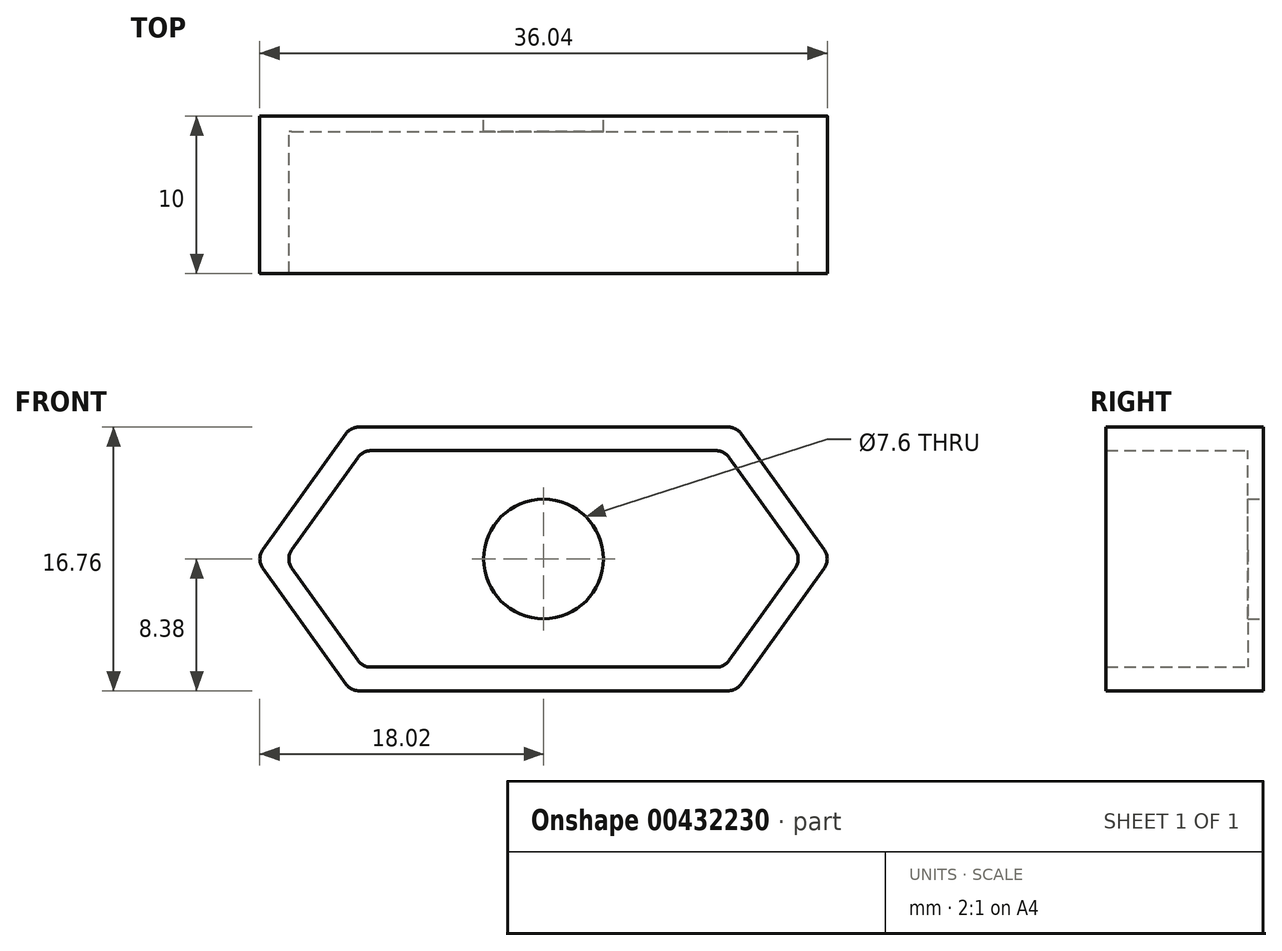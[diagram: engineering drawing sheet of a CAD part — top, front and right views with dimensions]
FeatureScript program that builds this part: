
annotation { "Feature Type Name" : "Feature", "Feature Type Description" : "" }
export const myFeature = defineFeature(function(context is Context, id is Id, definition is map)
    precondition{}
    {
        {
            var Q0;
            Q0=qCreatedBy(makeId("Front.planeOp"),FACE);
            var sketch = newSketch(context, id + "F0", { "sketchPlane" : qUnion([Q0])});
            skLineSegment(sketch, "E0.bottom", {"start": v(-11.74, 8.37) * mm, "end": v(12.25, 8.37) * mm});
            skLineSegment(sketch, "E0.top", {"start": v(-11.74, -8.37) * mm, "end": v(12.25, -8.37) * mm});
            skPoint(sketch, "E0.middle", {"position": v(0, 0) * mm});
            skLineSegment(sketch, "E1.bottom", {"start": v(-11.74, 8.38) * mm, "end": v(11.74, 8.38) * mm});
            skLineSegment(sketch, "E1.top", {"start": v(-11.74, -8.38) * mm, "end": v(11.74, -8.38) * mm});
            skPoint(sketch, "E2", {"position": v(-18.25, 0) * mm});
            skPoint(sketch, "E3", {"position": v(18.25, 0) * mm});
            skLineSegment(sketch, "E4", {"start": v(17.83, 0.58) * mm, "end": v(12.55, 7.96) * mm});
            skLineSegment(sketch, "E5", {"start": v(12.55, -7.96) * mm, "end": v(17.83, -0.58) * mm});
            skLineSegment(sketch, "E6", {"start": v(-17.83, 0.58) * mm, "end": v(-12.55, 7.96) * mm});
            skLineSegment(sketch, "E7", {"start": v(-17.83, -0.58) * mm, "end": v(-12.55, -7.96) * mm});
            skPoint(sketch, "E8.orphan", {"position": v(-18.25, 8.37) * mm});
            skPoint(sketch, "E9.orphan", {"position": v(-18.25, -8.37) * mm});
            skPoint(sketch, "E10.orphan", {"position": v(18.25, -8.37) * mm});
            skPoint(sketch, "E11.orphan", {"position": v(18.25, 8.37) * mm});
            skCircle(sketch, "E12", {"center": v(0, 0) * mm, "radius": 3.8 * mm});
            skLineSegment(sketch, "E13.0", {"start": v(-15.99, 0.58) * mm, "end": v(-11.78, 6.46) * mm});
            skLineSegment(sketch, "E14.0", {"start": v(-10.97, 6.87) * mm, "end": v(10.97, 6.87) * mm});
            skLineSegment(sketch, "E15.0", {"start": v(15.99, 0.58) * mm, "end": v(11.78, 6.46) * mm});
            skLineSegment(sketch, "E16.0", {"start": v(11.78, -6.46) * mm, "end": v(15.99, -0.58) * mm});
            skLineSegment(sketch, "E17.0", {"start": v(-10.97, -6.87) * mm, "end": v(10.97, -6.87) * mm});
            skLineSegment(sketch, "E18.0", {"start": v(-15.99, -0.58) * mm, "end": v(-11.78, -6.46) * mm});
            skPoint(sketch, "E19.visualSharp", {"position": v(-12.25, 8.38) * mm});
            skArc(sketch, "E19.filletArc", {"start": v(-11.74, 8.37) * mm, "mid": v(-12.2, 8.26) * mm, "end": v(-12.55, 7.96) * mm});
            skPoint(sketch, "E20.visualSharp", {"position": v(-11.48, 6.87) * mm});
            skArc(sketch, "E20.filletArc", {"start": v(-10.97, 6.87) * mm, "mid": v(-11.42, 6.76) * mm, "end": v(-11.78, 6.46) * mm});
            skPoint(sketch, "E21.visualSharp", {"position": v(-16.4, 0) * mm});
            skArc(sketch, "E21.filletArc", {"start": v(-15.99, 0.58) * mm, "mid": v(-16.17, 0) * mm, "end": v(-15.99, -0.58) * mm});
            skArc(sketch, "E22.filletArc", {"start": v(-17.83, 0.58) * mm, "mid": v(-18.02, 0) * mm, "end": v(-17.83, -0.58) * mm});
            skPoint(sketch, "E23.visualSharp", {"position": v(-11.48, -6.88) * mm});
            skArc(sketch, "E23.filletArc", {"start": v(-11.78, -6.46) * mm, "mid": v(-11.42, -6.76) * mm, "end": v(-10.97, -6.87) * mm});
            skPoint(sketch, "E24.visualSharp", {"position": v(-12.25, -8.38) * mm});
            skArc(sketch, "E24.filletArc", {"start": v(-12.55, -7.96) * mm, "mid": v(-12.2, -8.26) * mm, "end": v(-11.74, -8.38) * mm});
            skPoint(sketch, "E25.visualSharp", {"position": v(12.25, 8.38) * mm});
            skArc(sketch, "E25.filletArc", {"start": v(12.55, 7.96) * mm, "mid": v(12.2, 8.26) * mm, "end": v(11.74, 8.38) * mm});
            skPoint(sketch, "E26.visualSharp", {"position": v(11.48, 6.88) * mm});
            skArc(sketch, "E26.filletArc", {"start": v(11.78, 6.46) * mm, "mid": v(11.42, 6.76) * mm, "end": v(10.97, 6.87) * mm});
            skPoint(sketch, "E27.visualSharp", {"position": v(11.48, -6.87) * mm});
            skArc(sketch, "E27.filletArc", {"start": v(10.97, -6.87) * mm, "mid": v(11.42, -6.76) * mm, "end": v(11.78, -6.46) * mm});
            skPoint(sketch, "E28.visualSharp", {"position": v(12.25, -8.38) * mm});
            skArc(sketch, "E28.filletArc", {"start": v(11.74, -8.37) * mm, "mid": v(12.2, -8.26) * mm, "end": v(12.55, -7.96) * mm});
            skArc(sketch, "E29.filletArc", {"start": v(17.83, -0.58) * mm, "mid": v(18.02, 0) * mm, "end": v(17.83, 0.58) * mm});
            skPoint(sketch, "E30.visualSharp", {"position": v(16.4, 0) * mm});
            skArc(sketch, "E30.filletArc", {"start": v(15.99, -0.58) * mm, "mid": v(16.17, 0) * mm, "end": v(15.99, 0.58) * mm});
            skSolve(sketch);
        }
        {
            var Q0;
            Q0=makeQuery(id+"F0.imprint","IMPRINT",FACE,{"disambiguationData":[TD([[makeQuery(id+"F0.imprint","IMPRINT",EDGE,{"derivedFrom":sQuery(id+"F0.wireOp",EDGE,"E12")}),-1.0]])]});
            extrude(context, id + "F1", {"entities" : qUnion([Q0]), "depth" : 1 * mm});
        }
        {
            var Q0;
            Q0 = qSketchRegion(id + "F0", true);
            extrude(context, id + "F2", {"entities" : qUnion([Q0]), "operationType" : NewBodyOperationType.ADD, "depth" : 10 * mm});
        }
    });
